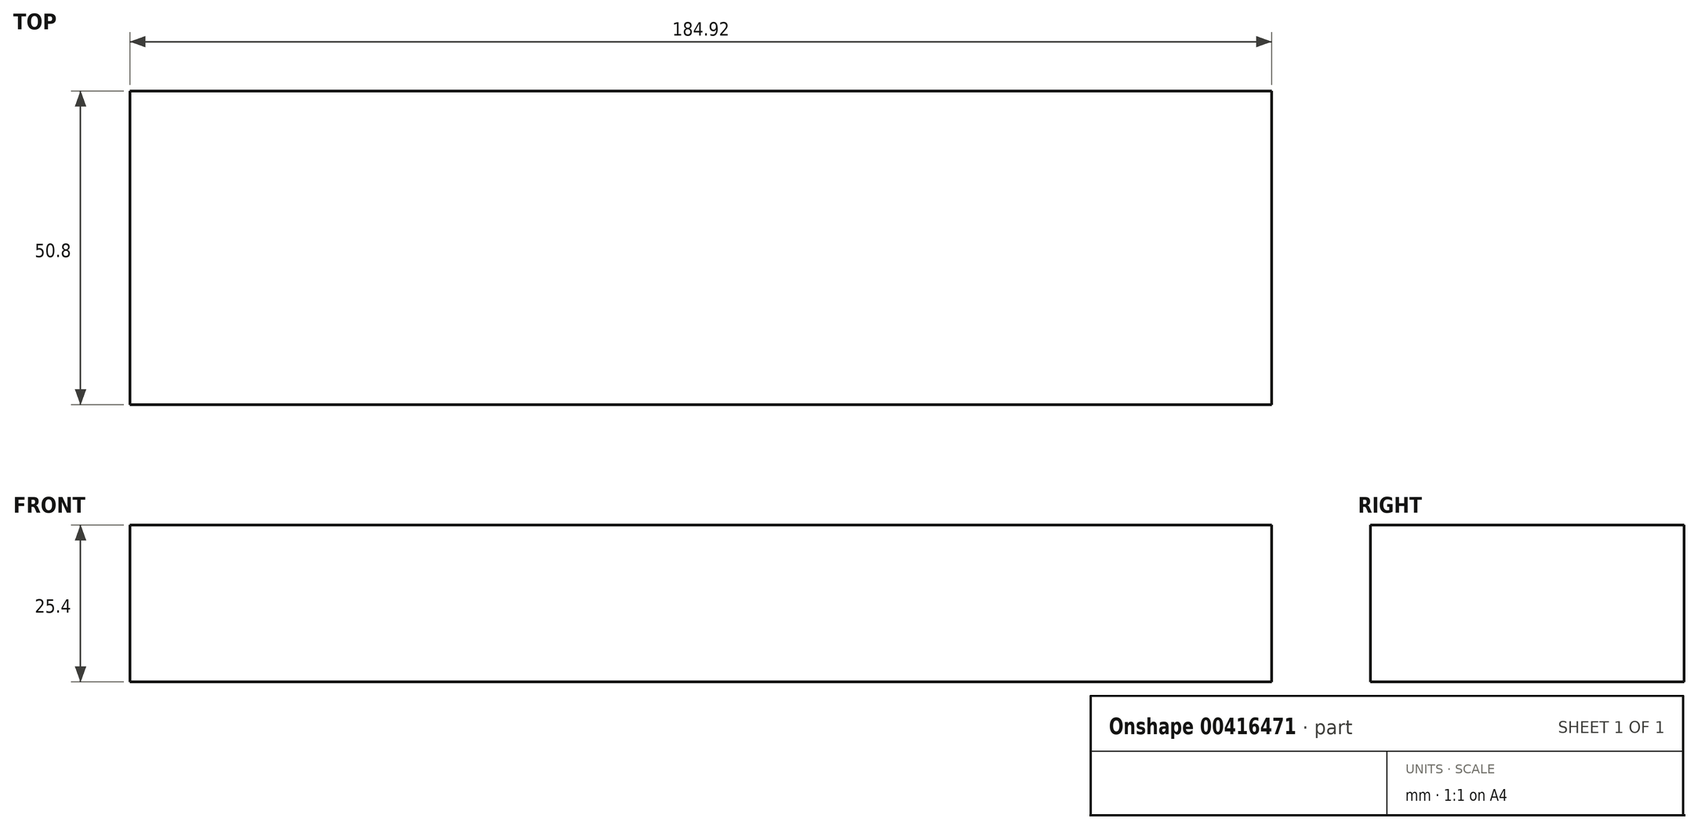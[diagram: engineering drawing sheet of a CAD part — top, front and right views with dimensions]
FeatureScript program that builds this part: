
annotation { "Feature Type Name" : "Feature", "Feature Type Description" : "" }
export const myFeature = defineFeature(function(context is Context, id is Id, definition is map)
    precondition{}
    {
        {
            var Q0;
            Q0=qCreatedBy(makeId("Top.planeOp"),FACE);
            var sketch = newSketch(context, id + "F0", { "sketchPlane" : qUnion([Q0])});
            skLineSegment(sketch, "E0", {"start": v(-71.68, 33.37) * mm, "end": v(113.24, 33.37) * mm});
            skLineSegment(sketch, "E1", {"start": v(113.24, 33.37) * mm, "end": v(113.24, -17.43) * mm});
            skLineSegment(sketch, "E2", {"start": v(113.24, -17.43) * mm, "end": v(-71.68, -17.43) * mm});
            skLineSegment(sketch, "E3", {"start": v(-71.68, -17.43) * mm, "end": v(-71.68, 33.37) * mm});
            skSolve(sketch);
        }
        {
            var Q0;
            Q0 = qSketchRegion(id + "F0", true);
            extrude(context, id + "F1", {"entities" : qUnion([Q0]), "depth" : 25.4 * mm});
        }
    });
